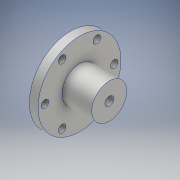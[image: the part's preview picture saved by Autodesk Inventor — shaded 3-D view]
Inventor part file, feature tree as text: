
AUTODESK INVENTOR PART (.ipt)
format: ipt  version: 2019 (Build 230136000, 136)  size: 131,584 bytes
history: native  units: mm
features: sketch x5, extrude x2, hole x2, other x1
ambient origin geometry x8: Origin, YZ Plane, XZ Plane, XY Plane, X Axis, Y Axis, Z Axis, Center Point
bodies: Body1 (feature_tree)
feature tree (10):
  other  "ソリッド1"
  sketch  "スケッチ1"
  extrude  "押し出し1"  Depth=56.8mm
  extrude  "押し出し2"  Depth=6.0mm TaperAngle=0.0deg
  hole  "穴2"  [1 undecoded]
  hole  "穴3"  [1 undecoded]
  sketch  "スケッチ2"
  sketch  "スケッチ3"
  sketch  "スケッチ7"
  sketch  "スケッチ8"
note: 2 required parameter values undecoded (feature->parameter linkage not recoverable at this tier; creation-order binding heuristic only, values carry confidence <= 0.55)
